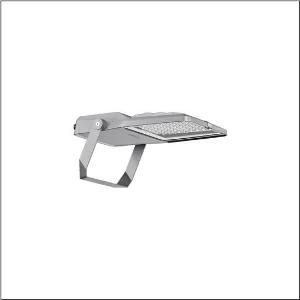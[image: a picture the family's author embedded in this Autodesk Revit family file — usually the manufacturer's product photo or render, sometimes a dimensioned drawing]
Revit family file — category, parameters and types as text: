
# Revit family: floodlight_fl_21_iq_mini___rs12_5xa7772c2b1a_7425
name_source: partatom
category: Lighting Fixtures
units: mm (PartAtom-declared; Revit-internal decimal feet)

## family parameters
Cut with Voids When Loaded = No
Host = Face
Light Source = No
Part Type = Normal
Room Calculation Point = No
Round Connector Dimension = Use Diameter
Shared = No

## types (1)
- --- (1 x LED, 12340 lm, 87.2 W, 3000K)
    Apparent Load = 87 VA
    CIE Flux Codes = 79 92 99 100 100
    Color Rendering = 70
    Color Temperature = 3000K
    Default Elevation = 1800 mm
    Description = Floodlight FL 21 iQ mini, floodlight, primary light control with lens, of PMMA, primary optical cover: protective disc, of toughened safety glass, transparent, light distribution: RS12, light emission: direct distribution, installation type: surface-mounted, LED, High Power LED, rated luminous flux: 12.340lm, luminous efficacy: 142lm/W, light colour: 730, colour temperature: 3000K, control: Street-Remote, Auto-Match, Temp-Guard, Night-Set, Smart-Wire, Desk-Remote (wireless, voltage-free reading and setting of iQ features in the workshop via application-optimized NFC function/RFID function), optimised constant luminous flux control (CLO 2.0), with terminal, 6-pole, mains connection: 220..240V, AC, 50/60Hz, start of lifetime: 87W, end of service life: 92W, reduction: 40W, luminaire housing, of diecast aluminium, powder-coated, Siteco® metallic grey (DB 702S), corrosivity category C5 mid according to DIN EN ISO 12944, sealing non-destructively replaceable, mounting bracket, of steel, galvanised, powder-coated, Siteco® metallic grey (DB 702S), protection rating (complete): IP66, insulation class (complete): insulation class II (safety insulation), certification: CE, ENEC, VDE, protection symbol: D, impact resistance: IK08, permissible operating ambient temperature: -40..+40°C, permissible operating ambient temperature for outdoor applications: -40..+50°C, standard: DIN EN 12944, LABS conformity tested according to VDMA 24364:2018-05, packaging unit: 1 piece

Light Distribution: RS12
    Height = 70 mm
    Lamp = 1 x LED
    Lamp Light Flux = 12340 lm
    Lamp Power = 87.2 W
    Lamp count = 1
    Length = 485 mm
    Luminous efficacy = 142 lm/W
    Manufacturer = Siteco
    ModVariant = No
    Model = 5XA7772C2B1A
    Number of Poles = 1
    OnlyDefault = Yes
    Power Factor = 1
    Product Name = Floodlight FL 21 iQ mini | RS12
    Product group = floodlight | pylon annexe
    ProductGroupID = 6200
    Protection Class = Protection class II
    Protection Degree = IP 66
    RLX_Detail_Level = 1
    RLX_Emergency_Light_Flux = 0 lm
    RLX_Emergency_Type = 0
    RLX_Emergency_Type_DB = No
    RlxData = <blob elided: 90977 chars, md5=baade4ba>
    Socket = socket
    Standby Power = 0 W
    System Light Flux = 12340 lm
    System Power = 87 W
    Type Comments = factory setting: luminous flux: 100 % | dim-lin: 254 | 456 mA
    Type Image = l_1006845.jpg
    URL = http://relux.com
    VarID = @adj_117803
    Voltage = 0 V
    Weight = 0.00 kg
    Width = 337 mm

## geometry (parser evidence)
native form markers: Blend x4, Sweep x16
no freeform markers — native parametric forms only
